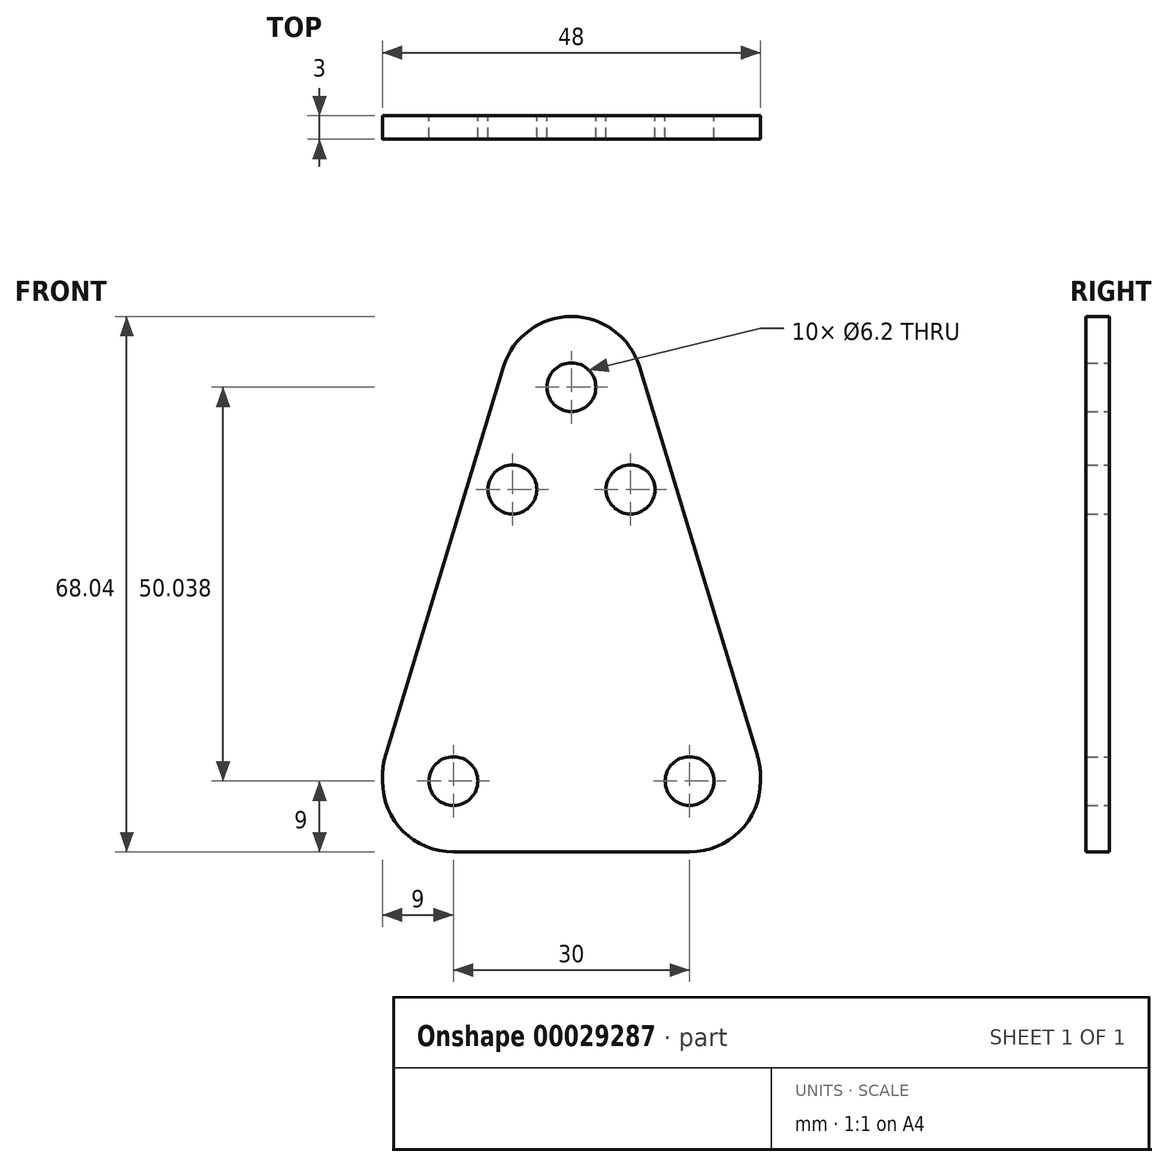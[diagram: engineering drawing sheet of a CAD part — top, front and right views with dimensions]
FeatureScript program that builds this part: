
annotation { "Feature Type Name" : "Feature", "Feature Type Description" : "" }
export const myFeature = defineFeature(function(context is Context, id is Id, definition is map)
    precondition{}
    {
        {
            var Q0;
            Q0=qCreatedBy(makeId("Front.planeOp"),FACE);
            var sketch = newSketch(context, id + "F0", { "sketchPlane" : qUnion([Q0])});
            skCircle(sketch, "E0", {"center": v(0, 0) * mm, "radius": 3.1 * mm});
            skCircle(sketch, "E1", {"center": v(30, 0) * mm, "radius": 3.1 * mm});
            skLineSegment(sketch, "E2", {"start": v(-9, 0.66) * mm, "end": v(-9, 0) * mm});
            skLineSegment(sketch, "E3", {"start": v(0, -9) * mm, "end": v(30, -9) * mm});
            skLineSegment(sketch, "E4", {"start": v(39, 0) * mm, "end": v(39, 0.66) * mm});
            skLineSegment(sketch, "E5", {"start": v(38.61, 3.28) * mm, "end": v(23.61, 52.65) * mm});
            skLineSegment(sketch, "E6", {"start": v(6.39, 52.65) * mm, "end": v(-8.61, 3.28) * mm});
            skPoint(sketch, "E7.visualSharp", {"position": v(-9, 2) * mm});
            skArc(sketch, "E7.filletArc", {"start": v(-8.61, 3.28) * mm, "mid": v(-8.9, 1.99) * mm, "end": v(-9, 0.66) * mm});
            skPoint(sketch, "E8.visualSharp", {"position": v(-9, -9) * mm});
            skArc(sketch, "E8.filletArc", {"start": v(-9, 0) * mm, "mid": v(-6.36, -6.36) * mm, "end": v(0, -9) * mm});
            skPoint(sketch, "E9.visualSharp", {"position": v(39, -9) * mm});
            skArc(sketch, "E9.filletArc", {"start": v(30, -9) * mm, "mid": v(36.36, -6.36) * mm, "end": v(39, 0) * mm});
            skPoint(sketch, "E10.visualSharp", {"position": v(39, 2) * mm});
            skArc(sketch, "E10.filletArc", {"start": v(39, 0.66) * mm, "mid": v(38.9, 1.99) * mm, "end": v(38.61, 3.28) * mm});
            skPoint(sketch, "E11.visualSharp", {"position": v(15, 81) * mm});
            skArc(sketch, "E11.filletArc", {"start": v(23.61, 52.65) * mm, "mid": v(15, 59.04) * mm, "end": v(6.39, 52.65) * mm});
            skCircle(sketch, "E12", {"center": v(15, 50.04) * mm, "radius": 3.1 * mm});
            skCircle(sketch, "E13", {"center": v(22.5, 37.05) * mm, "radius": 3.1 * mm});
            skCircle(sketch, "E14", {"center": v(7.5, 37.05) * mm, "radius": 3.1 * mm});
            skSolve(sketch);
        }
        {
            var Q0;
            Q0 = qSketchRegion(id + "F0", true);
            extrude(context, id + "F1", {"entities" : qUnion([Q0]), "depth" : 3 * mm});
        }
    });
